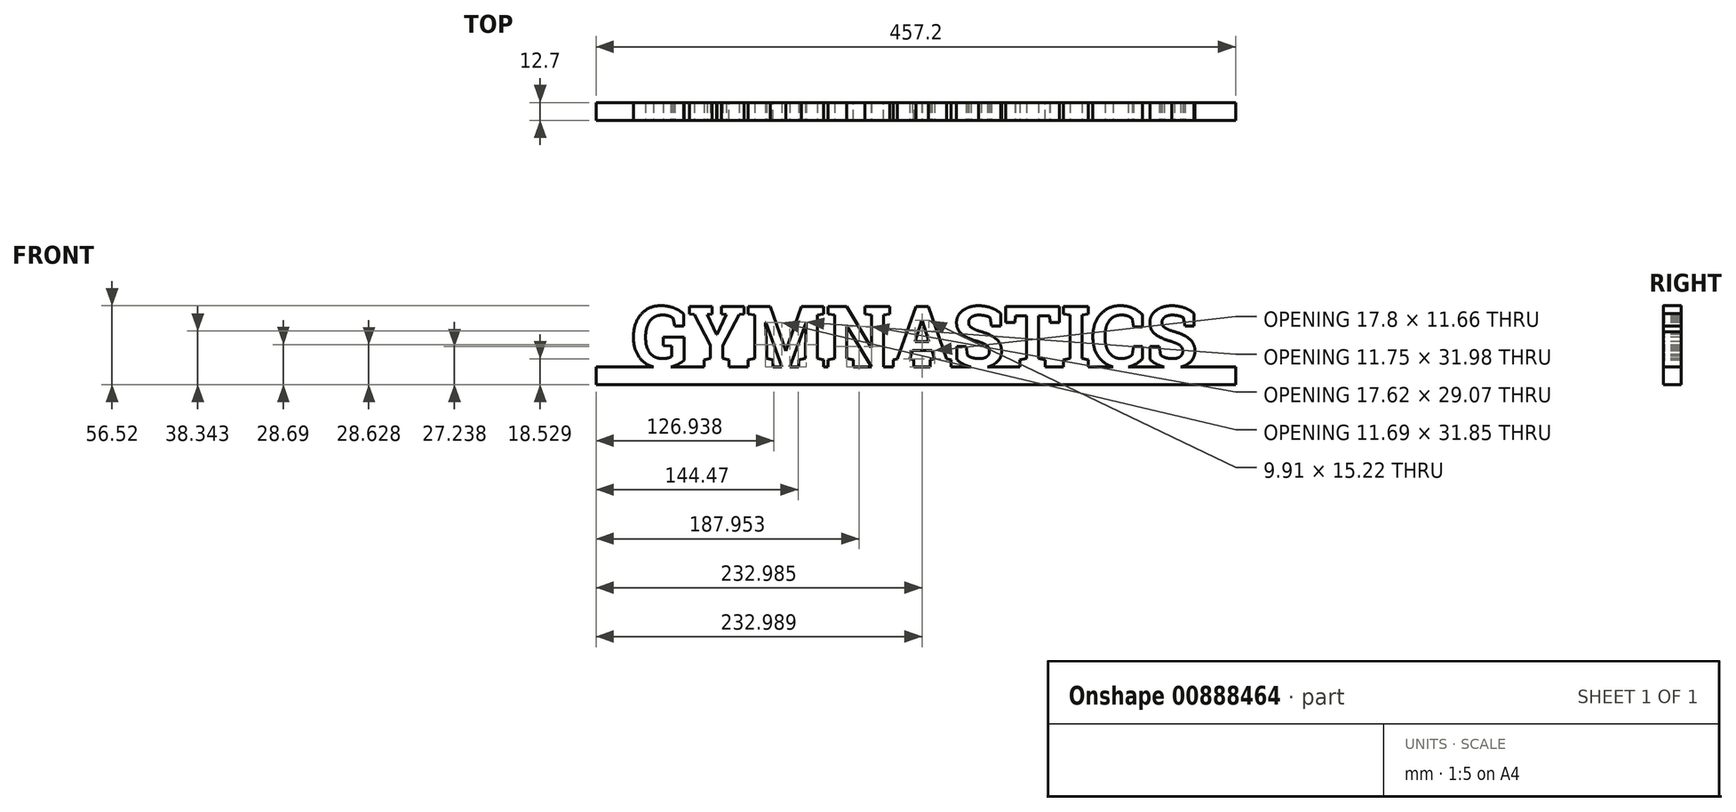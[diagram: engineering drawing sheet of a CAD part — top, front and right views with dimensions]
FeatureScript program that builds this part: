
annotation { "Feature Type Name" : "Feature", "Feature Type Description" : "" }
export const myFeature = defineFeature(function(context is Context, id is Id, definition is map)
    precondition{}
    {
        {
            var Q0;
            Q0=qCreatedBy(makeId("Front.planeOp"),FACE);
            var sketch = newSketch(context, id + "F0", { "sketchPlane" : qUnion([Q0])});
            skLineSegment(sketch, "E0.bottom", {"start": v(-211.92, -89.49) * mm, "end": v(245.28, -89.49) * mm});
            skLineSegment(sketch, "E0.top", {"start": v(-211.92, -102.19) * mm, "end": v(245.28, -102.19) * mm});
            skLineSegment(sketch, "E0.left", {"start": v(-211.92, -89.49) * mm, "end": v(-211.92, -102.19) * mm});
            skLineSegment(sketch, "E0.right", {"start": v(245.28, -89.49) * mm, "end": v(245.28, -102.19) * mm});
            skSolve(sketch);
        }
        {
            var Q0;
            Q0=makeQuery(id+"F0.imprint","IMPRINT",FACE,{"disambiguationData":[TD([[makeQuery(id+"F0.imprint","IMPRINT",EDGE,{"derivedFrom":sQuery(id+"F0.wireOp",EDGE,"E0.bottom")}),-1.0]])]});
            extrude(context, id + "F1", {"entities" : qUnion([Q0]), "depth" : 12.7 * mm, "offsetDistance" : 25.4 * mm});
        }
        {
            var Q0;
            Q0=makeQuery(id+"F1.opExtrude","CAP_FACE",FACE,{"disambiguationData":[OSD([sQuery(id+"F0.wireOp",EDGE,"E0.bottom"),sQuery(id+"F0.wireOp",EDGE,"E0.top"),sQuery(id+"F0.wireOp",EDGE,"E0.left"),sQuery(id+"F0.wireOp",EDGE,"E0.right")])],"isStart":false});
            var sketch = newSketch(context, id + "F2", { "sketchPlane" : qUnion([Q0])});
            skText(sketch, "E1", { "text": "GYMNASTICS", "fontName": "RobotoSlab-Bold.ttf"});
            skPoint(sketch, "E2", {"position": v(-186.52, -89.49) * mm});
            const initialGuessF2  = {"E1": [-0.18652, -0.08949, 1, 0, 0.04374]};
            skSetInitialGuess(sketch, initialGuessF2);
            skSolve(sketch);
        }
        {
            var Q0;
            Q0=qSketchRegion(id+"F2",true);
            extrude(context, id + "F3", {"entities" : qUnion([Q0]), "operationType" : NewBodyOperationType.ADD, "depth" : -12.7 * mm, "offsetDistance" : 25.4 * mm});
        }
    });
